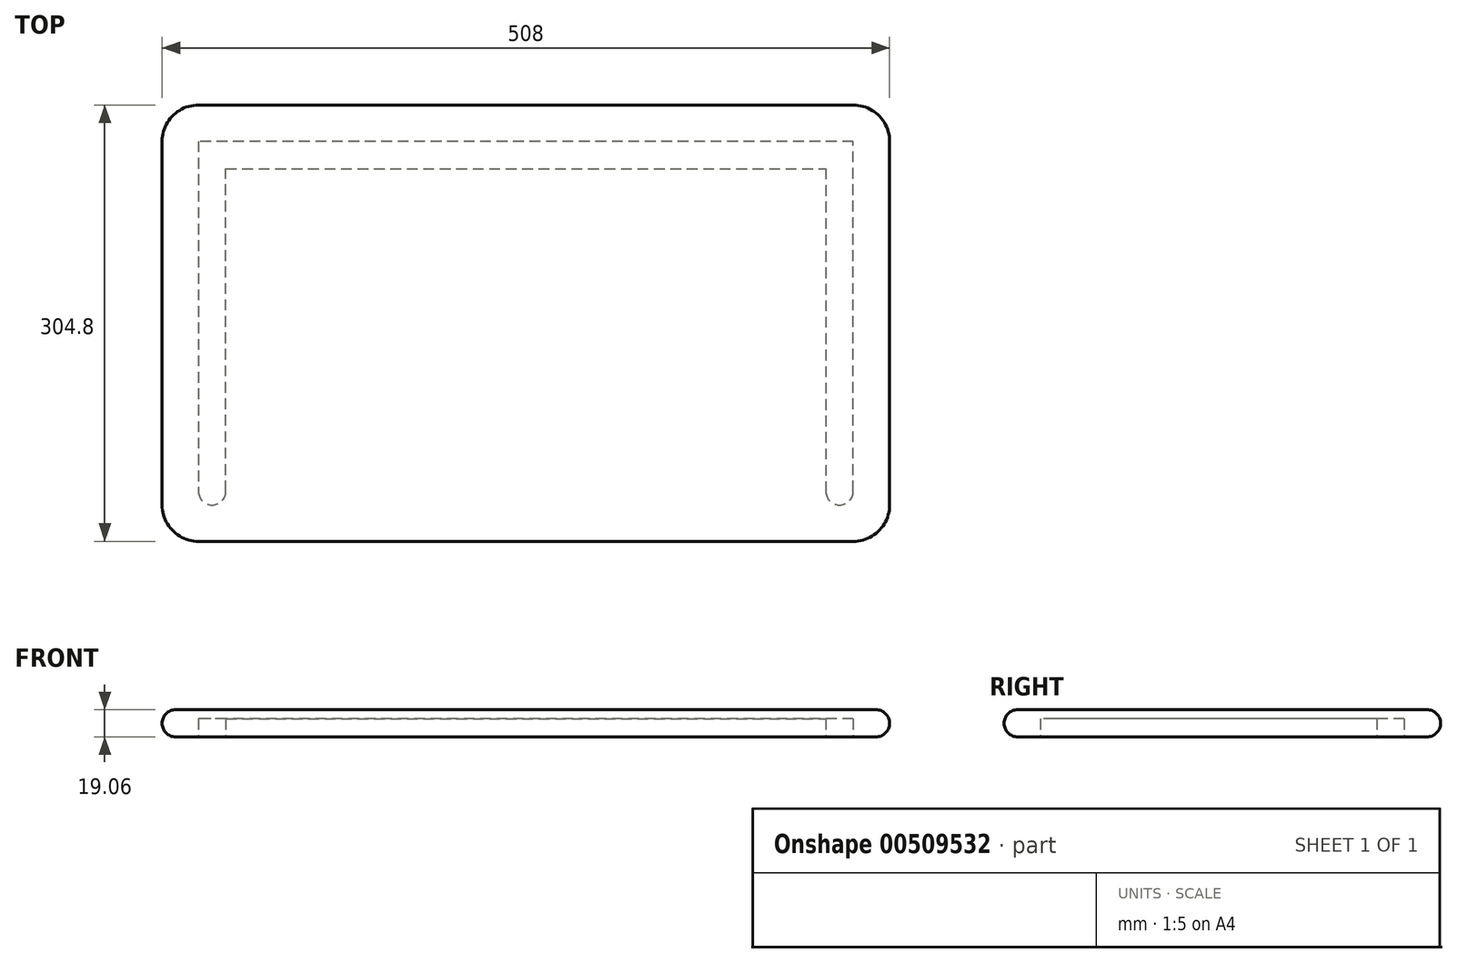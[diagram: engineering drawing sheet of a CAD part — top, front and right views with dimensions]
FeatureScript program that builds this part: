
annotation { "Feature Type Name" : "Feature", "Feature Type Description" : "" }
export const myFeature = defineFeature(function(context is Context, id is Id, definition is map)
    precondition{}
    {
        {
            var Q0;
            Q0=qCreatedBy(makeId("Top.planeOp"),FACE);
            var sketch = newSketch(context, id + "F0", { "sketchPlane" : qUnion([Q0])});
            skLineSegment(sketch, "E0.bottom", {"start": v(-228.6, 152.4) * mm, "end": v(228.6, 152.4) * mm});
            skLineSegment(sketch, "E0.top", {"start": v(-228.6, -152.4) * mm, "end": v(228.6, -152.4) * mm});
            skLineSegment(sketch, "E0.left", {"start": v(-254, 127) * mm, "end": v(-254, -127) * mm});
            skLineSegment(sketch, "E0.right", {"start": v(254, 127) * mm, "end": v(254, -127) * mm});
            skPoint(sketch, "E0.middle", {"position": v(0, 0) * mm});
            skPoint(sketch, "E1.visualSharp", {"position": v(-254, 152.4) * mm});
            skPoint(sketch, "E2.visualSharp", {"position": v(-254, -152.4) * mm});
            skArc(sketch, "E2.filletArc", {"start": v(-254, -127) * mm, "mid": v(-246.56, -144.96) * mm, "end": v(-228.6, -152.4) * mm});
            skPoint(sketch, "E3.visualSharp", {"position": v(254, -152.4) * mm});
            skArc(sketch, "E3.filletArc", {"start": v(228.6, -152.4) * mm, "mid": v(246.56, -144.96) * mm, "end": v(254, -127) * mm});
            skPoint(sketch, "E4.visualSharp", {"position": v(254, 152.4) * mm});
            skArc(sketch, "E5.filletArc", {"start": v(-228.6, 152.4) * mm, "mid": v(-246.56, 144.96) * mm, "end": v(-254, 127) * mm});
            skArc(sketch, "E6.filletArc", {"start": v(254, 127) * mm, "mid": v(246.56, 144.96) * mm, "end": v(228.6, 152.4) * mm});
            skSolve(sketch);
        }
        {
            var Q0;
            Q0=makeQuery(id+"F0.imprint","IMPRINT",FACE,{"disambiguationData":[TD([[makeQuery(id+"F0.imprint","IMPRINT",EDGE,{"derivedFrom":sQuery(id+"F0.wireOp",EDGE,"E0.bottom")}),-1.0]])]});
            extrude(context, id + "F1", {"entities" : qUnion([Q0]), "endBound" : BoundingType.SYMMETRIC, "depth" : 19.05 * mm, "offsetDistance" : 25.4 * mm});
        }
        {
            var Q0;
            Q0=makeQuery(id+"F1.opExtrude","CAP_EDGE",EDGE,{"disambiguationData":[OSD([sQuery(id+"F0.wireOp",EDGE,"E0.left")])],"isStart":false});
            var Q1;
            Q1=makeQuery(id+"F1.opExtrude","CAP_EDGE",EDGE,{"disambiguationData":[OSD([sQuery(id+"F0.wireOp",EDGE,"E0.top")])],"isStart":true});
            fillet(context, id + "F2", {"entities" : qUnion([Q0, Q1]), "radius" : 9.52 * mm, "tangentPropagation" : true, "allowEdgeOverflow" : false});
        }
        {
            var Q0;
            Q0=makeQuery(id+"F1.opExtrude","CAP_FACE",FACE,{"disambiguationData":[OSD([sQuery(id+"F0.wireOp",EDGE,"E0.bottom"),sQuery(id+"F0.wireOp",EDGE,"E0.top"),sQuery(id+"F0.wireOp",EDGE,"E0.left"),sQuery(id+"F0.wireOp",EDGE,"E0.right"),sQuery(id+"F0.wireOp",EDGE,"E2.filletArc"),sQuery(id+"F0.wireOp",EDGE,"E3.filletArc")])],"isStart":true});
            var sketch = newSketch(context, id + "F3", { "sketchPlane" : qUnion([Q0])});
            skLineSegment(sketch, "E7", {"start": v(-228.6, -127) * mm, "end": v(-228.6, 117.48) * mm});
            skLineSegment(sketch, "E8", {"start": v(-219.08, 127) * mm, "end": v(-219.08, 127) * mm});
            skLineSegment(sketch, "E9", {"start": v(-209.55, 117.48) * mm, "end": v(-209.55, -107.95) * mm});
            skLineSegment(sketch, "E10", {"start": v(-209.55, -107.95) * mm, "end": v(209.55, -107.95) * mm});
            skLineSegment(sketch, "E11", {"start": v(209.55, -107.95) * mm, "end": v(209.55, 117.48) * mm});
            skLineSegment(sketch, "E12", {"start": v(228.6, 117.48) * mm, "end": v(228.6, -127) * mm});
            skLineSegment(sketch, "E13", {"start": v(228.6, -127) * mm, "end": v(-228.6, -127) * mm});
            skPoint(sketch, "E14.visualSharp", {"position": v(-228.6, 127) * mm});
            skArc(sketch, "E14.filletArc", {"start": v(-219.08, 127) * mm, "mid": v(-225.81, 124.21) * mm, "end": v(-228.6, 117.48) * mm});
            skPoint(sketch, "E15.visualSharp", {"position": v(-209.55, 127) * mm});
            skArc(sketch, "E15.filletArc", {"start": v(-209.55, 117.48) * mm, "mid": v(-212.34, 124.21) * mm, "end": v(-219.08, 127) * mm});
            skPoint(sketch, "E16.visualSharp", {"position": v(209.55, 127) * mm});
            skPoint(sketch, "E17.visualSharp", {"position": v(228.6, 127) * mm});
            skPoint(sketch, "E18.endSnap0", {"position": v(0, -142.88) * mm});
            skLineSegment(sketch, "E19.trimOffspring", {"start": v(28.57, -127) * mm, "end": v(28.57, -152.4) * mm});
            skLineSegment(sketch, "E20", {"start": v(0, 0) * mm, "end": v(209.55, 0) * mm});
            skPoint(sketch, "E20.endSnap0", {"position": v(244.47, 0) * mm});
            skLineSegment(sketch, "E21", {"start": v(219.07, 127) * mm, "end": v(219.08, 127) * mm});
            skArc(sketch, "E22.filletArc", {"start": v(219.07, 127) * mm, "mid": v(212.34, 124.21) * mm, "end": v(209.55, 117.48) * mm});
            skArc(sketch, "E23.filletArc", {"start": v(228.6, 117.48) * mm, "mid": v(225.81, 124.21) * mm, "end": v(219.08, 127) * mm});
            skSolve(sketch);
        }
        {
            var Q0;
            Q0=makeQuery(id+"F3.imprint","IMPRINT",FACE,{"disambiguationData":[TD([[makeQuery(id+"F3.imprint","IMPRINT",EDGE,{"derivedFrom":sQuery(id+"F3.wireOp",EDGE,"E7")}),-1.0]])]});
            extrude(context, id + "F4", {"entities" : qUnion([Q0]), "operationType" : NewBodyOperationType.REMOVE, "oppositeDirection" : true, "depth" : 12.7 * mm});
        }
    });
